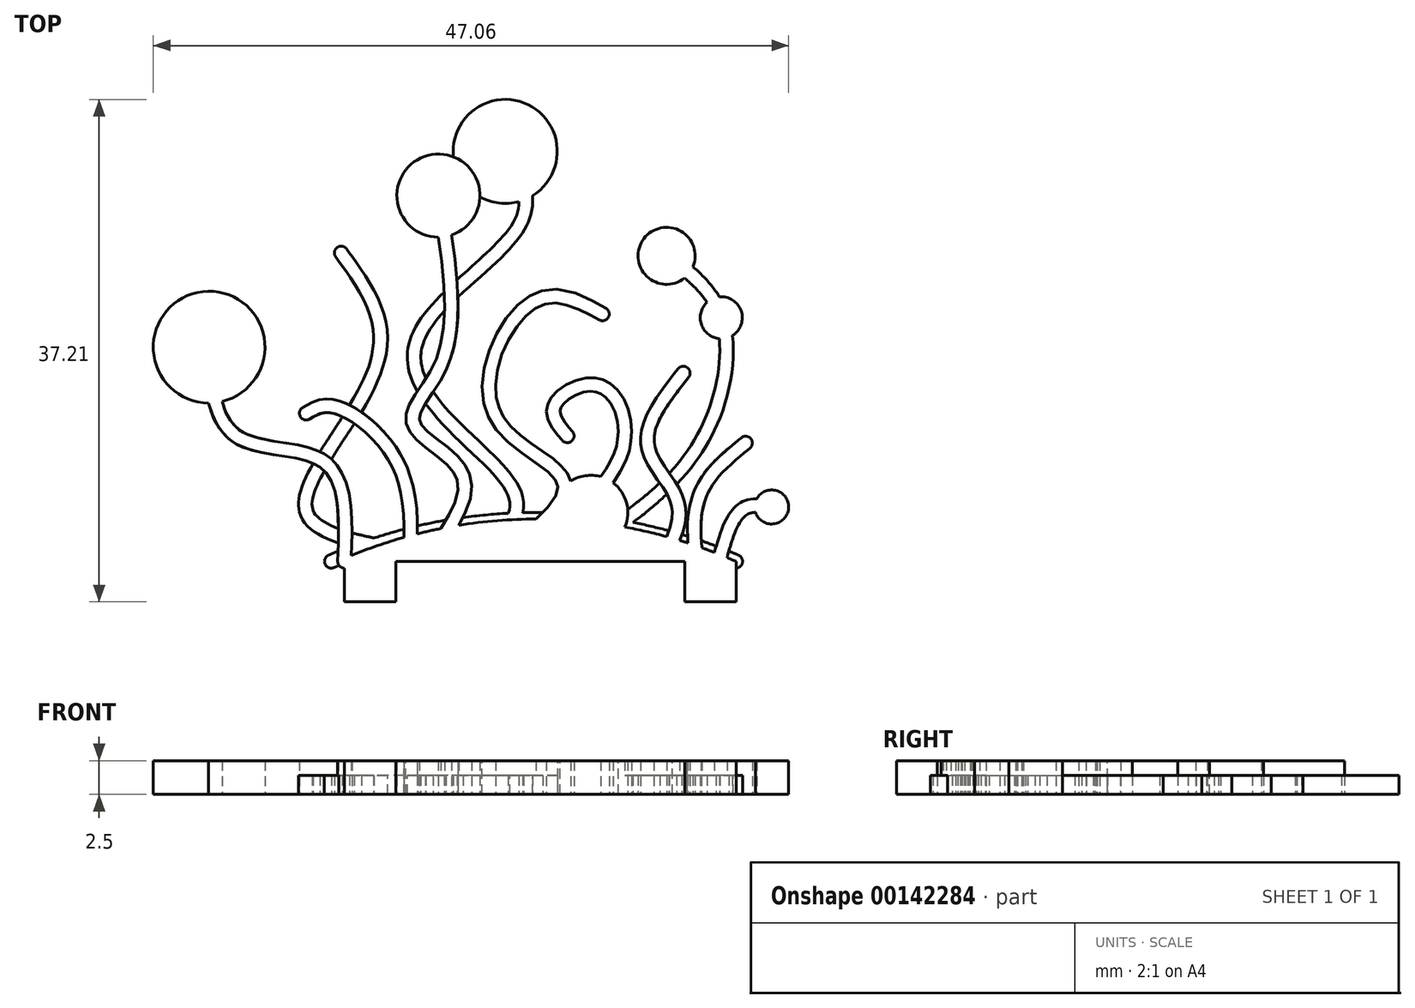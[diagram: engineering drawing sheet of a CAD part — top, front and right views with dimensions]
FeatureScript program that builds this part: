
annotation { "Feature Type Name" : "Feature", "Feature Type Description" : "" }
export const myFeature = defineFeature(function(context is Context, id is Id, definition is map)
    precondition{}
    {
        {
            var Q0;
            Q0=qCreatedBy(makeId("Top.planeOp"),FACE);
            var sketch = newSketch(context, id + "F0", { "sketchPlane" : qUnion([Q0])});
            skLineSegment(sketch, "E0", {"start": v(-14.04, 0) * mm, "end": v(14.96, 0) * mm});
            skLineSegment(sketch, "E1.bottom", {"start": v(-14.04, 0) * mm, "end": v(-10.24, 0) * mm});
            skLineSegment(sketch, "E1.top", {"start": v(-14.04, -3) * mm, "end": v(-10.24, -3) * mm});
            skLineSegment(sketch, "E1.left", {"start": v(-14.04, 0) * mm, "end": v(-14.04, -3) * mm});
            skLineSegment(sketch, "E1.right", {"start": v(-10.24, 0) * mm, "end": v(-10.24, -3) * mm});
            skLineSegment(sketch, "E2.bottom", {"start": v(14.96, 0) * mm, "end": v(11.16, 0) * mm});
            skLineSegment(sketch, "E2.top", {"start": v(14.96, -3) * mm, "end": v(11.16, -3) * mm});
            skLineSegment(sketch, "E2.left", {"start": v(14.96, 0) * mm, "end": v(14.96, -3) * mm});
            skLineSegment(sketch, "E2.right", {"start": v(11.16, 0) * mm, "end": v(11.16, -3) * mm});
            skLineSegment(sketch, "E3", {"start": v(-14.04, 0) * mm, "end": v(-10.24, -3) * mm, "construction": true});
            skLineSegment(sketch, "E4", {"start": v(-14.04, -3) * mm, "end": v(-10.24, 0) * mm, "construction": true});
            skLineSegment(sketch, "E5", {"start": v(11.16, 0) * mm, "end": v(14.96, -3) * mm, "construction": true});
            skLineSegment(sketch, "E6", {"start": v(11.16, -3) * mm, "end": v(14.96, 0) * mm, "construction": true});
            skPoint(sketch, "E7", {"position": v(-12.14, -1.5) * mm});
            skPoint(sketch, "E8", {"position": v(13.06, -1.5) * mm});
            skFitSpline(sketch, "E9", {"points": [v(-14.04, 0) * mm, v(-15.52, 7.32) * mm, v(-22, 9.28) * mm, v(-24.07, 15.87) * mm], "startDerivative": vector(0.84, 26.47) * mm, "endDerivative": vector(-1.6, 24.7) * mm});
            skFitSpline(sketch, "E10", {"points": [v(-8, 0) * mm, v(-5.33, 6.5) * mm, v(-8.93, 10.2) * mm, v(-6.87, 14.63) * mm, v(-7.08, 27.09) * mm], "startDerivative": vector(20.9, 28.72) * mm, "endDerivative": vector(-6.86, 42.4) * mm});
            skFitSpline(sketch, "E11", {"points": [v(-3.1, 0) * mm, v(2.21, 5.87) * mm, v(-3, 11.07) * mm, v(0, 19.24) * mm, v(5.07, 18.32) * mm], "startDerivative": vector(33.34, 24.23) * mm, "endDerivative": vector(24.38, -13.02) * mm});
            skFitSpline(sketch, "E12", {"points": [v(-9.22, 0) * mm, v(-10.24, 7.5) * mm, v(-14.93, 11.48) * mm, v(-16.87, 10.97) * mm], "startDerivative": vector(0.72, 19.06) * mm, "endDerivative": vector(-7.95, -4.62) * mm});
            skFitSpline(sketch, "E13", {"points": [v(12.01, 0) * mm, v(12.34, 5.05) * mm, v(15.67, 8.77) * mm], "startDerivative": vector(-0.87, 10.72) * mm, "endDerivative": vector(8.19, 6.82) * mm});
            skFitSpline(sketch, "E14", {"points": [v(13.7, 0) * mm, v(15.42, 3.82) * mm, v(17.6, 4.03) * mm], "startDerivative": vector(2.31, 8.35) * mm, "endDerivative": vector(5.67, -0.78) * mm});
            skFitSpline(sketch, "E15", {"points": [v(9.45, 0) * mm, v(10.64, 4.34) * mm, v(8.43, 8.58) * mm, v(11.06, 13.95) * mm], "startDerivative": vector(7.45, 14.12) * mm, "endDerivative": vector(11.96, 15.37) * mm});
            skFitSpline(sketch, "E16", {"points": [v(6.7, 0) * mm, v(4.2, 3.63) * mm, v(6.58, 8.46) * mm, v(4.85, 13) * mm, v(1.51, 11.5) * mm, v(2.47, 9.3) * mm], "startDerivative": vector(-18.74, 17.03) * mm, "endDerivative": vector(12.14, -14.22) * mm});
            skArc(sketch, "E17.0.startCap", {"start": v(-13.54, -0.02) * mm, "mid": v(-14.06, -0.5) * mm, "end": v(-14.54, 0.02) * mm});
            skArc(sketch, "E17.0.endCap", {"start": v(-24.56, 15.83) * mm, "mid": v(-24.1, 16.37) * mm, "end": v(-23.57, 15.9) * mm});
            skFitSpline(sketch, "E17.0.left", {"points": [v(-14.54, 0.02) * mm, v(-14.52, 0.57) * mm, v(-14.49, 1.66) * mm, v(-14.5, 3.22) * mm, v(-14.63, 4.63) * mm, v(-14.94, 5.8) * mm, v(-15.37, 6.52) * mm, v(-15.81, 6.94) * mm, v(-16.23, 7.2) * mm, v(-16.75, 7.4) * mm, v(-17.53, 7.62) * mm, v(-18.65, 7.8) * mm, v(-19.83, 7.99) * mm, v(-20.75, 8.2) * mm, v(-21.41, 8.4) * mm, v(-22.04, 8.69) * mm, v(-22.6, 9.08) * mm, v(-23.07, 9.56) * mm, v(-23.57, 10.3) * mm, v(-24, 11.35) * mm, v(-24.3, 12.77) * mm, v(-24.46, 14.28) * mm, v(-24.53, 15.32) * mm, v(-24.56, 15.83) * mm]});
            skFitSpline(sketch, "E17.0.right", {"points": [v(-13.54, -0.02) * mm, v(-13.52, 0.54) * mm, v(-13.49, 1.64) * mm, v(-13.5, 3.26) * mm, v(-13.64, 4.79) * mm, v(-13.94, 5.93) * mm, v(-14.33, 6.74) * mm, v(-14.72, 7.28) * mm, v(-15.21, 7.75) * mm, v(-15.8, 8.1) * mm, v(-16.43, 8.35) * mm, v(-17.33, 8.6) * mm, v(-18.5, 8.8) * mm, v(-19.65, 8.98) * mm, v(-20.5, 9.17) * mm, v(-21.06, 9.34) * mm, v(-21.55, 9.57) * mm, v(-21.95, 9.84) * mm, v(-22.29, 10.2) * mm, v(-22.67, 10.75) * mm, v(-23.03, 11.63) * mm, v(-23.4, 13.34) * mm, v(-23.5, 14.87) * mm, v(-23.57, 15.9) * mm]});
            skArc(sketch, "E17.1.startCap", {"start": v(-9.72, 0) * mm, "mid": v(-9.72, 0) * mm, "end": v(-9.72, 0.02) * mm});
            skArc(sketch, "E17.1.endCap", {"start": v(-16.62, 10.54) * mm, "mid": v(-17.3, 10.72) * mm, "end": v(-17.12, 11.4) * mm});
            skFitSpline(sketch, "E17.1.left", {"points": [v(-9.72, 0.02) * mm, v(-9.69, 0.81) * mm, v(-9.63, 2.39) * mm, v(-9.73, 4.26) * mm, v(-10.02, 5.67) * mm, v(-10.36, 6.67) * mm, v(-10.86, 7.62) * mm, v(-11.52, 8.53) * mm, v(-12.29, 9.35) * mm, v(-13.1, 10.05) * mm, v(-13.8, 10.5) * mm, v(-14.3, 10.76) * mm, v(-14.66, 10.9) * mm, v(-14.98, 10.99) * mm, v(-15.24, 11.02) * mm, v(-15.48, 11.01) * mm, v(-15.78, 10.96) * mm, v(-16.14, 10.81) * mm, v(-16.46, 10.63) * mm, v(-16.62, 10.54) * mm]});
            skFitSpline(sketch, "E17.1.right", {"points": [v(-8.72, -0.02) * mm, v(-8.69, 0.78) * mm, v(-8.63, 2.38) * mm, v(-8.74, 4.37) * mm, v(-9.05, 5.93) * mm, v(-9.38, 6.87) * mm, v(-9.72, 7.6) * mm, v(-10.13, 8.33) * mm, v(-10.75, 9.17) * mm, v(-11.6, 10.08) * mm, v(-12.5, 10.85) * mm, v(-13.43, 11.46) * mm, v(-14.18, 11.8) * mm, v(-14.77, 11.97) * mm, v(-15.33, 12.04) * mm, v(-15.97, 11.96) * mm, v(-16.6, 11.7) * mm, v(-16.96, 11.5) * mm, v(-17.12, 11.4) * mm]});
            skArc(sketch, "E17.2.startCap", {"start": v(-8.5, 0) * mm, "mid": v(-8.48, 0.15) * mm, "end": v(-8.41, 0.3) * mm});
            skArc(sketch, "E17.2.endCap", {"start": v(-7.57, 27) * mm, "mid": v(-7.16, 27.58) * mm, "end": v(-6.59, 27.17) * mm});
            skFitSpline(sketch, "E17.2.left", {"points": [v(-8.41, 0.3) * mm, v(-7.97, 0.9) * mm, v(-7.33, 1.78) * mm, v(-6.6, 2.92) * mm, v(-6.14, 3.74) * mm, v(-5.81, 4.5) * mm, v(-5.64, 5.2) * mm, v(-5.62, 5.7) * mm, v(-5.7, 6.06) * mm, v(-5.79, 6.31) * mm, v(-5.93, 6.57) * mm, v(-6.2, 6.92) * mm, v(-6.64, 7.36) * mm, v(-7.29, 7.88) * mm, v(-7.97, 8.4) * mm, v(-8.5, 8.83) * mm, v(-8.89, 9.2) * mm, v(-9.13, 9.5) * mm, v(-9.34, 9.84) * mm, v(-9.47, 10.21) * mm, v(-9.5, 10.6) * mm, v(-9.46, 10.97) * mm, v(-9.35, 11.32) * mm, v(-9.15, 11.78) * mm, v(-8.83, 12.33) * mm, v(-8.37, 13) * mm, v(-7.9, 13.73) * mm, v(-7.47, 14.49) * mm, v(-7.13, 15.3) * mm, v(-6.9, 16.22) * mm, v(-6.69, 17.54) * mm, v(-6.63, 19.38) * mm, v(-6.8, 21.8) * mm, v(-7.15, 24.36) * mm, v(-7.43, 26.12) * mm, v(-7.57, 27) * mm]});
            skFitSpline(sketch, "E17.2.right", {"points": [v(-7.6, -0.3) * mm, v(-7.17, 0.3) * mm, v(-6.5, 1.2) * mm, v(-5.74, 2.4) * mm, v(-5.25, 3.29) * mm, v(-4.87, 4.17) * mm, v(-4.64, 5.04) * mm, v(-4.62, 5.76) * mm, v(-4.73, 6.33) * mm, v(-4.88, 6.75) * mm, v(-5.1, 7.13) * mm, v(-5.46, 7.6) * mm, v(-5.99, 8.12) * mm, v(-6.68, 8.67) * mm, v(-7.36, 9.19) * mm, v(-7.85, 9.59) * mm, v(-8.15, 9.89) * mm, v(-8.32, 10.1) * mm, v(-8.43, 10.28) * mm, v(-8.48, 10.43) * mm, v(-8.5, 10.58) * mm, v(-8.48, 10.76) * mm, v(-8.41, 10.97) * mm, v(-8.27, 11.3) * mm, v(-7.99, 11.78) * mm, v(-7.54, 12.45) * mm, v(-7.05, 13.2) * mm, v(-6.65, 13.9) * mm, v(-6.37, 14.52) * mm, v(-6.13, 15.17) * mm, v(-5.91, 16.02) * mm, v(-5.69, 17.47) * mm, v(-5.63, 19.4) * mm, v(-5.8, 21.9) * mm, v(-6.16, 24.51) * mm, v(-6.44, 26.28) * mm, v(-6.59, 27.17) * mm]});
            skArc(sketch, "E17.3.startCap", {"start": v(-3.6, 0) * mm, "mid": v(-3.54, 0.23) * mm, "end": v(-3.39, 0.4) * mm});
            skArc(sketch, "E17.3.endCap", {"start": v(5.3, 18.76) * mm, "mid": v(5.51, 18.08) * mm, "end": v(4.83, 17.88) * mm});
            skFitSpline(sketch, "E17.3.left", {"points": [v(-3.39, 0.4) * mm, v(-2.7, 0.9) * mm, v(-1.66, 1.66) * mm, v(-0.43, 2.64) * mm, v(0.38, 3.35) * mm, v(1.04, 4.02) * mm, v(1.51, 4.64) * mm, v(1.72, 5.1) * mm, v(1.77, 5.4) * mm, v(1.77, 5.58) * mm, v(1.73, 5.76) * mm, v(1.63, 5.96) * mm, v(1.47, 6.18) * mm, v(1.16, 6.5) * mm, v(0.65, 6.93) * mm, v(-0.12, 7.48) * mm, v(-0.97, 8.07) * mm, v(-1.82, 8.74) * mm, v(-2.6, 9.5) * mm, v(-3.15, 10.24) * mm, v(-3.48, 10.92) * mm, v(-3.72, 11.64) * mm, v(-3.85, 12.59) * mm, v(-3.79, 13.77) * mm, v(-3.54, 14.94) * mm, v(-3.13, 16.09) * mm, v(-2.6, 17.16) * mm, v(-1.96, 18.13) * mm, v(-1.24, 18.95) * mm, v(-0.59, 19.49) * mm, v(-0.03, 19.8) * mm, v(0.55, 20.02) * mm, v(1.27, 20.15) * mm, v(2.4, 20.07) * mm, v(3.76, 19.58) * mm, v(4.8, 19.03) * mm, v(5.3, 18.76) * mm]});
            skFitSpline(sketch, "E17.3.right", {"points": [v(-2.8, -0.4) * mm, v(-2.1, 0.1) * mm, v(-1.06, 0.86) * mm, v(0.2, 1.87) * mm, v(1.06, 2.61) * mm, v(1.8, 3.36) * mm, v(2.36, 4.1) * mm, v(2.67, 4.74) * mm, v(2.78, 5.29) * mm, v(2.77, 5.7) * mm, v(2.67, 6.12) * mm, v(2.48, 6.5) * mm, v(2.23, 6.83) * mm, v(1.83, 7.25) * mm, v(1.24, 7.73) * mm, v(0.45, 8.3) * mm, v(-0.38, 8.88) * mm, v(-1.17, 9.5) * mm, v(-1.86, 10.17) * mm, v(-2.3, 10.78) * mm, v(-2.55, 11.3) * mm, v(-2.74, 11.85) * mm, v(-2.84, 12.62) * mm, v(-2.8, 13.63) * mm, v(-2.5, 15.02) * mm, v(-1.92, 16.38) * mm, v(-1.16, 17.53) * mm, v(-0.54, 18.24) * mm, v(0.1, 18.75) * mm, v(0.7, 19.03) * mm, v(1.31, 19.14) * mm, v(1.95, 19.1) * mm, v(2.63, 18.92) * mm, v(3.58, 18.55) * mm, v(4.33, 18.15) * mm, v(4.83, 17.88) * mm]});
            skArc(sketch, "E17.4.startCap", {"start": v(7.04, 0.37) * mm, "mid": v(7.16, 0.2) * mm, "end": v(7.2, 0) * mm});
            skArc(sketch, "E17.4.endCap", {"start": v(2.85, 9.62) * mm, "mid": v(2.8, 8.91) * mm, "end": v(2.09, 8.97) * mm});
            skFitSpline(sketch, "E17.4.left", {"points": [v(6.37, -0.37) * mm, v(5.98, -0.02) * mm, v(5.38, 0.52) * mm, v(4.68, 1.28) * mm, v(4.23, 1.87) * mm, v(3.88, 2.5) * mm, v(3.71, 3.06) * mm, v(3.68, 3.55) * mm, v(3.73, 4.03) * mm, v(3.93, 4.6) * mm, v(4.27, 5.25) * mm, v(4.69, 5.9) * mm, v(5.12, 6.54) * mm, v(5.53, 7.2) * mm, v(5.87, 7.87) * mm, v(6.08, 8.44) * mm, v(6.17, 8.91) * mm, v(6.22, 9.4) * mm, v(6.2, 10.27) * mm, v(5.95, 11.21) * mm, v(5.52, 11.93) * mm, v(5.2, 12.26) * mm, v(4.92, 12.43) * mm, v(4.71, 12.52) * mm, v(4.48, 12.57) * mm, v(4.14, 12.6) * mm, v(3.66, 12.53) * mm, v(3.08, 12.32) * mm, v(2.56, 12.01) * mm, v(2.23, 11.72) * mm, v(2.06, 11.49) * mm, v(1.98, 11.34) * mm, v(1.94, 11.22) * mm, v(1.93, 11.06) * mm, v(1.98, 10.83) * mm, v(2.17, 10.46) * mm, v(2.47, 10.06) * mm, v(2.72, 9.77) * mm, v(2.85, 9.62) * mm]});
            skFitSpline(sketch, "E17.4.right", {"points": [v(7.04, 0.37) * mm, v(6.65, 0.72) * mm, v(6.07, 1.25) * mm, v(5.44, 1.93) * mm, v(5.06, 2.43) * mm, v(4.8, 2.9) * mm, v(4.7, 3.25) * mm, v(4.69, 3.52) * mm, v(4.71, 3.8) * mm, v(4.84, 4.2) * mm, v(5.13, 4.74) * mm, v(5.64, 5.54) * mm, v(6.26, 6.44) * mm, v(6.8, 7.46) * mm, v(7.04, 8.17) * mm, v(7.16, 8.76) * mm, v(7.22, 9.37) * mm, v(7.2, 10.12) * mm, v(7.05, 11) * mm, v(6.75, 11.82) * mm, v(6.33, 12.54) * mm, v(5.85, 13.03) * mm, v(5.4, 13.32) * mm, v(5.02, 13.48) * mm, v(4.62, 13.57) * mm, v(4.08, 13.6) * mm, v(3.4, 13.5) * mm, v(2.65, 13.23) * mm, v(1.98, 12.83) * mm, v(1.52, 12.42) * mm, v(1.23, 12.05) * mm, v(1.06, 11.74) * mm, v(0.95, 11.4) * mm, v(0.92, 10.96) * mm, v(1.04, 10.44) * mm, v(1.34, 9.9) * mm, v(1.7, 9.42) * mm, v(1.96, 9.12) * mm, v(2.09, 8.97) * mm]});
            skArc(sketch, "E17.5.startCap", {"start": v(8.95, 0) * mm, "mid": v(8.96, 0.12) * mm, "end": v(9, 0.23) * mm});
            skArc(sketch, "E17.5.endCap", {"start": v(10.66, 14.26) * mm, "mid": v(11.37, 14.34) * mm, "end": v(11.45, 13.64) * mm});
            skFitSpline(sketch, "E17.5.left", {"points": [v(9, 0.23) * mm, v(9.32, 0.82) * mm, v(9.77, 1.69) * mm, v(10.14, 2.76) * mm, v(10.24, 3.39) * mm, v(10.23, 3.86) * mm, v(10.17, 4.2) * mm, v(10.06, 4.54) * mm, v(9.82, 5.02) * mm, v(9.42, 5.66) * mm, v(8.85, 6.46) * mm, v(8.4, 7.18) * mm, v(8.12, 7.8) * mm, v(7.97, 8.28) * mm, v(7.9, 8.8) * mm, v(7.9, 9.32) * mm, v(8, 9.83) * mm, v(8.2, 10.5) * mm, v(8.59, 11.34) * mm, v(9.2, 12.32) * mm, v(9.91, 13.3) * mm, v(10.41, 13.94) * mm, v(10.66, 14.26) * mm]});
            skFitSpline(sketch, "E17.5.right", {"points": [v(9.89, -0.23) * mm, v(10.04, 0.06) * mm, v(10.36, 0.66) * mm, v(10.79, 1.57) * mm, v(11.11, 2.5) * mm, v(11.25, 3.3) * mm, v(11.23, 3.95) * mm, v(11.14, 4.45) * mm, v(10.98, 4.92) * mm, v(10.7, 5.52) * mm, v(10.24, 6.23) * mm, v(9.68, 7.03) * mm, v(9.28, 7.67) * mm, v(9.06, 8.16) * mm, v(8.94, 8.52) * mm, v(8.9, 8.86) * mm, v(8.9, 9.34) * mm, v(9.07, 9.99) * mm, v(9.46, 10.85) * mm, v(10.03, 11.75) * mm, v(10.7, 12.68) * mm, v(11.2, 13.32) * mm, v(11.45, 13.64) * mm]});
            skArc(sketch, "E17.6.startCap", {"start": v(12.51, 0.04) * mm, "mid": v(12.51, 0.02) * mm, "end": v(12.51, 0) * mm});
            skArc(sketch, "E17.6.endCap", {"start": v(15.35, 9.15) * mm, "mid": v(16.05, 9.1) * mm, "end": v(15.99, 8.39) * mm});
            skFitSpline(sketch, "E17.6.left", {"points": [v(11.51, -0.04) * mm, v(11.48, 0.4) * mm, v(11.4, 1.3) * mm, v(11.37, 2.66) * mm, v(11.46, 3.76) * mm, v(11.64, 4.6) * mm, v(11.86, 5.23) * mm, v(12.15, 5.82) * mm, v(12.62, 6.55) * mm, v(13.34, 7.39) * mm, v(14.32, 8.3) * mm, v(15, 8.87) * mm, v(15.35, 9.15) * mm]});
            skFitSpline(sketch, "E17.6.right", {"points": [v(12.51, 0.04) * mm, v(12.48, 0.49) * mm, v(12.4, 1.37) * mm, v(12.37, 2.64) * mm, v(12.45, 3.62) * mm, v(12.61, 4.34) * mm, v(12.78, 4.85) * mm, v(13.02, 5.32) * mm, v(13.41, 5.94) * mm, v(14.05, 6.68) * mm, v(14.97, 7.54) * mm, v(15.65, 8.1) * mm, v(15.99, 8.39) * mm]});
            skArc(sketch, "E17.7.startCap", {"start": v(13.2, 0) * mm, "mid": v(13.2, 0.07) * mm, "end": v(13.22, 0.13) * mm});
            skArc(sketch, "E17.7.endCap", {"start": v(17.66, 4.53) * mm, "mid": v(18.1, 3.96) * mm, "end": v(17.53, 3.54) * mm});
            skFitSpline(sketch, "E17.7.left", {"points": [v(13.22, 0.13) * mm, v(13.31, 0.48) * mm, v(13.5, 1.18) * mm, v(13.83, 2.2) * mm, v(14.14, 2.95) * mm, v(14.44, 3.5) * mm, v(14.7, 3.85) * mm, v(15.02, 4.16) * mm, v(15.39, 4.4) * mm, v(15.77, 4.55) * mm, v(16.3, 4.64) * mm, v(16.94, 4.63) * mm, v(17.43, 4.56) * mm, v(17.66, 4.53) * mm]});
            skFitSpline(sketch, "E17.7.right", {"points": [v(14.18, -0.13) * mm, v(14.28, 0.21) * mm, v(14.47, 0.9) * mm, v(14.77, 1.86) * mm, v(15.05, 2.53) * mm, v(15.3, 2.96) * mm, v(15.48, 3.2) * mm, v(15.66, 3.39) * mm, v(15.83, 3.5) * mm, v(16.03, 3.58) * mm, v(16.35, 3.64) * mm, v(16.84, 3.63) * mm, v(17.3, 3.57) * mm, v(17.53, 3.54) * mm]});
            skArc(sketch, "E18", {"start": v(14.96, 0) * mm, "mid": v(0.21, 3.13) * mm, "end": v(-14.54, 0.02) * mm});
            skCircle(sketch, "E19", {"center": v(-7.08, 27.09) * mm, "radius": 3.08 * mm});
            skCircle(sketch, "E20", {"center": v(-24.07, 15.87) * mm, "radius": 4.14 * mm});
            skCircle(sketch, "E21", {"center": v(17.6, 4.03) * mm, "radius": 1.26 * mm});
            skCircle(sketch, "E22", {"center": v(4.2, 3.63) * mm, "radius": 2.75 * mm});
            skSolve(sketch);
        }
        {
            var Q0;
            Q0 = qSketchRegion(id + "F0", true);
            var Q1;
            {var subQ0=sQuery(id+"F0.wireOp",EDGE,"E22");var subQ1=sQuery(id+"F0.wireOp",EDGE,"E11");var subQ2=makeQuery(id+"F0.imprint","INTERSECT",VERTEX,{"disambiguationData":[OD(0.0)],"derivedFrom":[subQ1,subQ0]});Q1=makeQuery(id+"F0.imprint","IMPRINT",FACE,{"disambiguationData":[TD([[makeQuery(id+"F0.imprint","IMPRINT",EDGE,{"disambiguationData":[TD([[subQ2,1.0]])],"derivedFrom":subQ1}),1.0]])]});}
            var Q2;
            {var subQ0=sQuery(id+"F0.wireOp",EDGE,"E18");var subQ1=sQuery(id+"F0.wireOp",EDGE,"E11");var subQ2=makeQuery(id+"F0.imprint","INTERSECT",VERTEX,{"derivedFrom":[subQ1,subQ0]});Q2=makeQuery(id+"F0.imprint","IMPRINT",FACE,{"disambiguationData":[TD([[makeQuery(id+"F0.imprint","IMPRINT",EDGE,{"disambiguationData":[TD([[subQ2,-1.0]])],"derivedFrom":subQ1}),-1.0]])]});}
            var Q3;
            {var subQ0=sQuery(id+"F0.wireOp",EDGE,"E22");var subQ1=sQuery(id+"F0.wireOp",EDGE,"E17.3.right");var subQ2=makeQuery(id+"F0.imprint","INTERSECT",VERTEX,{"disambiguationData":[OD(1.0)],"derivedFrom":[subQ1,subQ0]});Q3=makeQuery(id+"F0.imprint","IMPRINT",FACE,{"disambiguationData":[TD([[makeQuery(id+"F0.imprint","IMPRINT",EDGE,{"disambiguationData":[TD([[subQ2,-1.0]])],"derivedFrom":subQ1}),-1.0]])]});}
            var Q4;
            {var subQ0=sQuery(id+"F0.wireOp",EDGE,"E22");var subQ1=sQuery(id+"F0.wireOp",EDGE,"E16");var subQ2=makeQuery(id+"F0.imprint","INTERSECT",VERTEX,{"disambiguationData":[OD(1.0)],"derivedFrom":[subQ1,subQ0]});Q4=makeQuery(id+"F0.imprint","IMPRINT",FACE,{"disambiguationData":[TD([[makeQuery(id+"F0.imprint","IMPRINT",EDGE,{"disambiguationData":[TD([[subQ2,-1.0]])],"derivedFrom":subQ1}),1.0]])]});}
            var Q5;
            {var subQ0=sQuery(id+"F0.wireOp",EDGE,"E22");var subQ1=sQuery(id+"F0.wireOp",EDGE,"E16");var subQ2=makeQuery(id+"F0.imprint","INTERSECT",VERTEX,{"disambiguationData":[OD(1.0)],"derivedFrom":[subQ1,subQ0]});Q5=makeQuery(id+"F0.imprint","IMPRINT",FACE,{"disambiguationData":[TD([[makeQuery(id+"F0.imprint","IMPRINT",EDGE,{"disambiguationData":[TD([[subQ2,-1.0]])],"derivedFrom":subQ1}),-1.0]])]});}
            var Q6;
            {var subQ0=sQuery(id+"F0.wireOp",EDGE,"E22");var subQ1=sQuery(id+"F0.wireOp",EDGE,"E17.3.right");var subQ2=makeQuery(id+"F0.imprint","INTERSECT",VERTEX,{"disambiguationData":[OD(1.0)],"derivedFrom":[subQ1,subQ0]});Q6=makeQuery(id+"F0.imprint","IMPRINT",FACE,{"disambiguationData":[TD([[makeQuery(id+"F0.imprint","IMPRINT",EDGE,{"disambiguationData":[TD([[subQ2,-1.0]])],"derivedFrom":subQ1}),1.0]])]});}
            extrude(context, id + "F1", {"entities" : qUnion([Q0, Q1, Q2, Q3, Q4, Q5, Q6]), "depth" : 2.5 * mm});
        }
        {
            var Q0;
            Q0=qCreatedBy(makeId("Top.planeOp"),FACE);
            var sketch = newSketch(context, id + "F2", { "sketchPlane" : qUnion([Q0])});
            skArc(sketch, "E23.0", {"start": v(0.13, 3.13) * mm, "mid": v(-2.74, 3.02) * mm, "end": v(-5.6, 2.67) * mm, "construction": true});
            skArc(sketch, "E24.0", {"start": v(-6.91, 2.43) * mm, "mid": v(-7.79, 2.25) * mm, "end": v(-8.66, 2.04) * mm, "construction": true});
            skArc(sketch, "E25.0", {"start": v(-9.67, 1.77) * mm, "mid": v(-11.61, 1.16) * mm, "end": v(-13.53, 0.45) * mm, "construction": true});
            skLineSegment(sketch, "E26.0", {"start": v(6.86, 2.52) * mm, "end": v(6.86, 2.52) * mm});
            skArc(sketch, "E27.0", {"start": v(13.36, 0.66) * mm, "mid": v(12.9, 0.84) * mm, "end": v(12.44, 1.01) * mm, "construction": true});
            skPoint(sketch, "E28.2.internal.snap0", {"position": v(-11.61, 1.16) * mm});
            skFitSpline(sketch, "E28", {"points": [v(-11.61, 1.16) * mm, v(-16.92, 4.06) * mm, v(-11.61, 14.85) * mm, v(-14.28, 22.85) * mm], "startDerivative": vector(-27.72, 6.37) * mm, "endDerivative": vector(-15.83, 22.3) * mm});
            skPoint(sketch, "E29.1.internal.snap0", {"position": v(-2.74, 3.02) * mm});
            skFitSpline(sketch, "E29", {"points": [v(-1.6, 3.1) * mm, v(-2.74, 6.86) * mm, v(-8.85, 15.57) * mm, v(-1.02, 25.09) * mm, v(-2.13, 30.36) * mm], "startDerivative": vector(11.45, 20.23) * mm, "endDerivative": vector(-15.1, 24.24) * mm});
            skFitSpline(sketch, "E30", {"points": [v(6.2, 2.64) * mm, v(12.48, 9.12) * mm, v(13.87, 18.04) * mm, v(9.82, 22.63) * mm], "startDerivative": vector(20.14, 15.8) * mm, "endDerivative": vector(-17.38, 13.02) * mm});
            skArc(sketch, "E31.0.startCap", {"start": v(-11.5, 1.65) * mm, "mid": v(-11.15, 1.35) * mm, "end": v(-11.2, 0.9) * mm});
            skArc(sketch, "E31.0.endCap", {"start": v(-14.7, 22.56) * mm, "mid": v(-14.57, 23.26) * mm, "end": v(-13.88, 23.14) * mm});
            skFitSpline(sketch, "E31.0.left", {"points": [v(-11.73, 0.68) * mm, v(-12.3, 0.8) * mm, v(-13.47, 1.08) * mm, v(-14.82, 1.48) * mm, v(-15.76, 1.9) * mm, v(-16.4, 2.29) * mm, v(-16.92, 2.76) * mm, v(-17.23, 3.26) * mm, v(-17.38, 3.71) * mm, v(-17.43, 4.08) * mm, v(-17.43, 4.46) * mm, v(-17.36, 4.96) * mm, v(-17.16, 5.6) * mm, v(-16.8, 6.42) * mm, v(-16.35, 7.27) * mm, v(-15.65, 8.44) * mm, v(-14.65, 9.99) * mm, v(-13.66, 11.56) * mm, v(-12.97, 12.8) * mm, v(-12.53, 13.71) * mm, v(-12.2, 14.59) * mm, v(-11.99, 15.4) * mm, v(-11.9, 16.19) * mm, v(-11.93, 17.19) * mm, v(-12.2, 18.39) * mm, v(-12.85, 19.8) * mm, v(-13.7, 21.17) * mm, v(-14.36, 22.1) * mm, v(-14.7, 22.56) * mm]});
            skFitSpline(sketch, "E31.0.right", {"points": [v(-11.5, 1.65) * mm, v(-12.08, 1.78) * mm, v(-13.23, 2.05) * mm, v(-14.5, 2.43) * mm, v(-15.3, 2.8) * mm, v(-15.8, 3.1) * mm, v(-16.15, 3.42) * mm, v(-16.32, 3.7) * mm, v(-16.4, 3.94) * mm, v(-16.44, 4.2) * mm, v(-16.41, 4.62) * mm, v(-16.23, 5.25) * mm, v(-15.91, 5.97) * mm, v(-15.49, 6.77) * mm, v(-14.8, 7.9) * mm, v(-13.81, 9.44) * mm, v(-12.6, 11.37) * mm, v(-11.74, 13) * mm, v(-11.24, 14.27) * mm, v(-10.92, 15.54) * mm, v(-10.87, 17.05) * mm, v(-11.26, 18.73) * mm, v(-11.97, 20.28) * mm, v(-12.88, 21.74) * mm, v(-13.55, 22.67) * mm, v(-13.88, 23.14) * mm]});
            skArc(sketch, "E31.1.startCap", {"start": v(-2.1, 3.05) * mm, "mid": v(-2.1, 3.06) * mm, "end": v(-2.1, 3.06) * mm});
            skArc(sketch, "E31.1.endCap", {"start": v(-2.56, 30.1) * mm, "mid": v(-2.4, 30.79) * mm, "end": v(-1.7, 30.63) * mm});
            skFitSpline(sketch, "E31.1.left", {"points": [v(-2.04, 3.34) * mm, v(-1.94, 3.51) * mm, v(-1.81, 3.84) * mm, v(-1.78, 4.3) * mm, v(-1.9, 4.79) * mm, v(-2.18, 5.36) * mm, v(-2.64, 6) * mm, v(-3.48, 6.95) * mm, v(-4.9, 8.31) * mm, v(-6.47, 9.84) * mm, v(-7.61, 11.14) * mm, v(-8.36, 12.16) * mm, v(-8.96, 13.2) * mm, v(-9.27, 14.13) * mm, v(-9.38, 14.88) * mm, v(-9.38, 15.46) * mm, v(-9.28, 16.04) * mm, v(-9.05, 16.79) * mm, v(-8.58, 17.68) * mm, v(-7.8, 18.71) * mm, v(-6.89, 19.71) * mm, v(-5.88, 20.68) * mm, v(-4.84, 21.63) * mm, v(-3.83, 22.55) * mm, v(-2.9, 23.45) * mm, v(-2.12, 24.3) * mm, v(-1.54, 25.1) * mm, v(-1.22, 25.83) * mm, v(-1.1, 26.51) * mm, v(-1.16, 27.2) * mm, v(-1.36, 27.9) * mm, v(-1.79, 28.85) * mm, v(-2.24, 29.6) * mm, v(-2.56, 30.1) * mm]});
            skFitSpline(sketch, "E31.1.right", {"points": [v(-1.17, 2.84) * mm, v(-1.03, 3.1) * mm, v(-0.82, 3.6) * mm, v(-0.77, 4.39) * mm, v(-0.95, 5.15) * mm, v(-1.33, 5.9) * mm, v(-1.86, 6.63) * mm, v(-2.54, 7.4) * mm, v(-3.35, 8.21) * mm, v(-4.53, 9.34) * mm, v(-6.06, 10.84) * mm, v(-7.35, 12.4) * mm, v(-8.04, 13.63) * mm, v(-8.3, 14.38) * mm, v(-8.38, 14.96) * mm, v(-8.38, 15.38) * mm, v(-8.3, 15.8) * mm, v(-8.13, 16.38) * mm, v(-7.74, 17.13) * mm, v(-6.8, 18.38) * mm, v(-5.23, 19.95) * mm, v(-3.47, 21.51) * mm, v(-2.2, 22.74) * mm, v(-1.35, 23.66) * mm, v(-0.8, 24.42) * mm, v(-0.46, 25.06) * mm, v(-0.23, 25.69) * mm, v(-0.1, 26.48) * mm, v(-0.2, 27.7) * mm, v(-0.76, 29.09) * mm, v(-1.4, 30.12) * mm, v(-1.7, 30.63) * mm]});
            skArc(sketch, "E31.2.startCap", {"start": v(5.7, 2.67) * mm, "mid": v(5.7, 2.7) * mm, "end": v(5.7, 2.71) * mm});
            skArc(sketch, "E31.2.endCap", {"start": v(9.52, 22.23) * mm, "mid": v(9.42, 22.93) * mm, "end": v(10.12, 23.03) * mm});
            skFitSpline(sketch, "E31.2.left", {"points": [v(5.89, 3.03) * mm, v(6.73, 3.69) * mm, v(8.4, 5) * mm, v(10.26, 6.79) * mm, v(11.51, 8.44) * mm, v(12.32, 9.81) * mm, v(12.97, 11.35) * mm, v(13.44, 12.96) * mm, v(13.7, 14.57) * mm, v(13.75, 16.11) * mm, v(13.55, 17.5) * mm, v(13.12, 18.67) * mm, v(12.45, 19.68) * mm, v(11.6, 20.59) * mm, v(10.6, 21.42) * mm, v(9.88, 21.96) * mm, v(9.52, 22.23) * mm]});
            skFitSpline(sketch, "E31.2.right", {"points": [v(6.5, 2.24) * mm, v(7.35, 2.9) * mm, v(8.61, 3.9) * mm, v(10.21, 5.36) * mm, v(11.33, 6.55) * mm, v(12.18, 7.66) * mm, v(12.78, 8.62) * mm, v(13.33, 9.64) * mm, v(13.91, 11.01) * mm, v(14.41, 12.73) * mm, v(14.7, 14.47) * mm, v(14.75, 16.15) * mm, v(14.57, 17.47) * mm, v(14.28, 18.44) * mm, v(13.88, 19.34) * mm, v(13.23, 20.32) * mm, v(11.95, 21.66) * mm, v(10.84, 22.49) * mm, v(10.12, 23.03) * mm]});
            skArc(sketch, "E32", {"start": v(14.94, 0) * mm, "mid": v(10.95, 1.47) * mm, "end": v(6.81, 2.48) * mm});
            skArc(sketch, "E33.0.startCap", {"start": v(15.14, 0.46) * mm, "mid": v(15.4, -0.2) * mm, "end": v(14.74, -0.46) * mm});
            skArc(sketch, "E33.0.endCap", {"start": v(-14.82, -0.46) * mm, "mid": v(-15.48, -0.2) * mm, "end": v(-15.22, 0.46) * mm});
            skArc(sketch, "E33.0.left", {"start": v(14.74, -0.46) * mm, "mid": v(-0.04, 2.6) * mm, "end": v(-14.82, -0.46) * mm});
            skArc(sketch, "E33.0.right", {"start": v(15.14, 0.46) * mm, "mid": v(-0.04, 3.6) * mm, "end": v(-15.22, 0.46) * mm});
            skPoint(sketch, "E34.orphan", {"position": v(4.85, 2.84) * mm});
            skArc(sketch, "E35.trimOffspring", {"start": v(5.7, 2.67) * mm, "mid": v(-4.85, 2.8) * mm, "end": v(-15.02, 0) * mm});
            skPoint(sketch, "E36.orphan", {"position": v(9.8, 1.84) * mm});
            skCircle(sketch, "E37", {"center": v(9.82, 22.63) * mm, "radius": 2.11 * mm});
            skCircle(sketch, "E38", {"center": v(13.87, 18.04) * mm, "radius": 1.56 * mm});
            skCircle(sketch, "E39", {"center": v(-2.13, 30.36) * mm, "radius": 3.85 * mm});
            skFitSpline(sketch, "E40.trimOffspring", {"points": [v(-1.17, 2.84) * mm, v(-1.03, 3.1) * mm, v(-0.82, 3.6) * mm, v(-0.77, 4.39) * mm, v(-0.95, 5.15) * mm, v(-1.33, 5.9) * mm, v(-1.86, 6.63) * mm, v(-2.54, 7.4) * mm, v(-3.35, 8.21) * mm, v(-4.53, 9.34) * mm, v(-6.06, 10.84) * mm, v(-7.35, 12.4) * mm, v(-8.04, 13.63) * mm, v(-8.3, 14.38) * mm, v(-8.38, 14.96) * mm, v(-8.38, 15.38) * mm, v(-8.3, 15.8) * mm, v(-8.13, 16.38) * mm, v(-7.74, 17.13) * mm, v(-6.8, 18.38) * mm, v(-5.23, 19.95) * mm, v(-3.47, 21.51) * mm, v(-2.2, 22.74) * mm, v(-1.35, 23.66) * mm, v(-0.8, 24.42) * mm, v(-0.46, 25.06) * mm, v(-0.23, 25.69) * mm, v(-0.1, 26.48) * mm, v(-0.2, 27.7) * mm, v(-0.76, 29.09) * mm, v(-1.4, 30.12) * mm, v(-1.7, 30.63) * mm]});
            skSolve(sketch);
        }
        {
            var Q0;
            Q0 = qSketchRegion(id + "F2", true);
            extrude(context, id + "F3", {"entities" : qUnion([Q0]), "operationType" : NewBodyOperationType.ADD, "depth" : 1.4 * mm});
        }
    });
